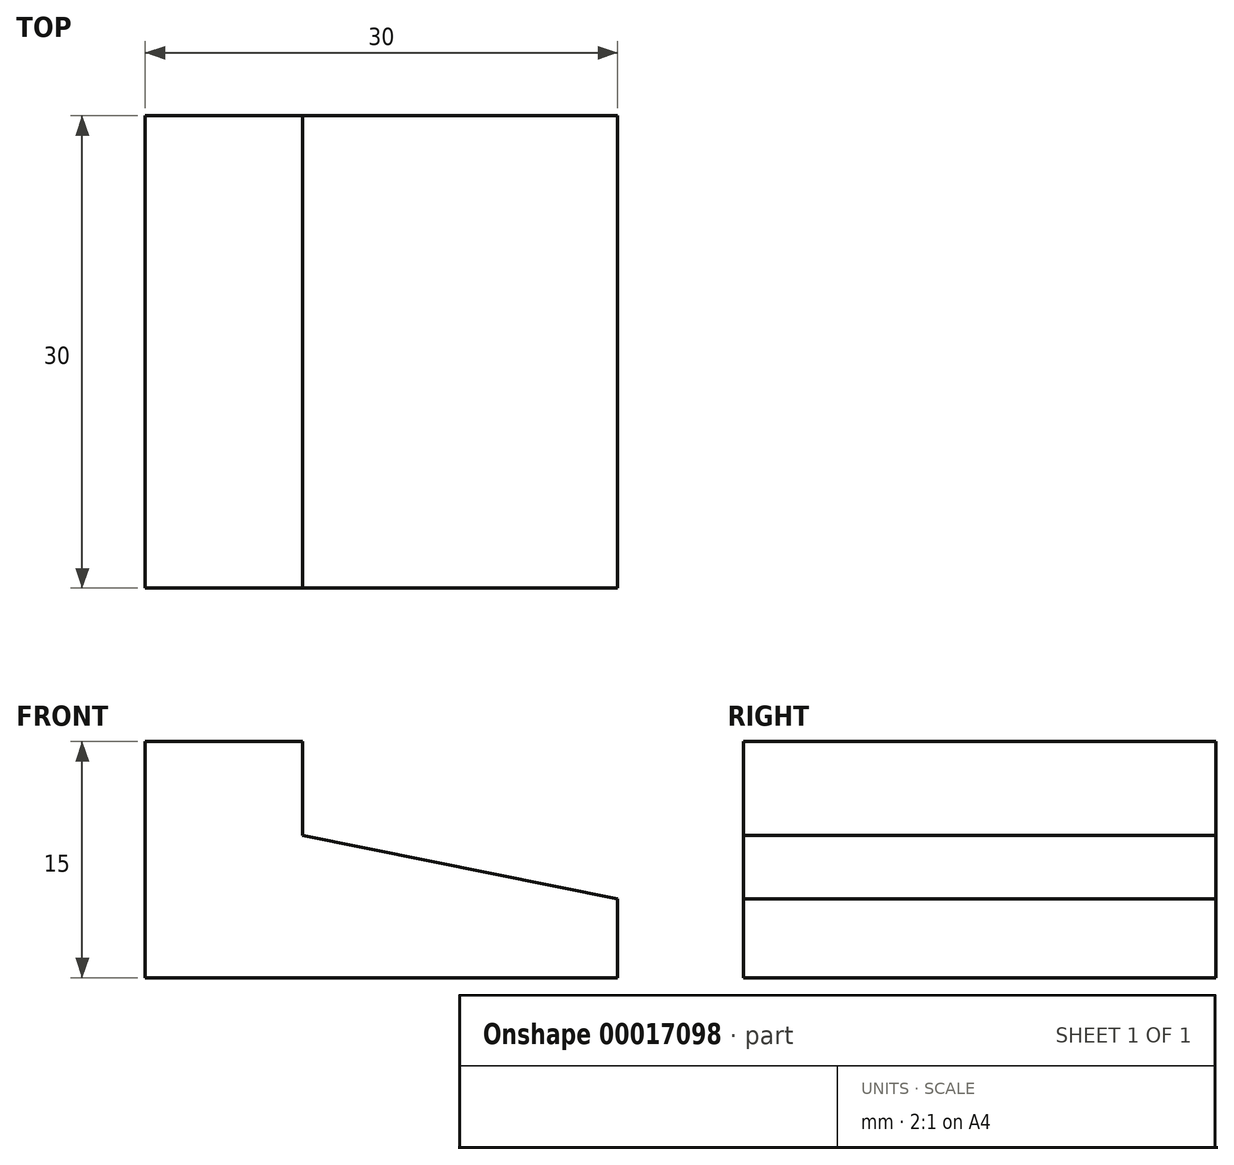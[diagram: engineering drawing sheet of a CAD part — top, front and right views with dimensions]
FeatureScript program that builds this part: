
annotation { "Feature Type Name" : "Feature", "Feature Type Description" : "" }
export const myFeature = defineFeature(function(context is Context, id is Id, definition is map)
    precondition{}
    {
        {
            var Q0;
            Q0=qCreatedBy(makeId("Front.planeOp"),FACE);
            var sketch = newSketch(context, id + "F0", { "sketchPlane" : qUnion([Q0])});
            skLineSegment(sketch, "E0", {"start": v(5.16, 8.93) * mm, "end": v(-4.84, 8.93) * mm});
            skLineSegment(sketch, "E1", {"start": v(-4.84, 8.93) * mm, "end": v(-4.84, -6.07) * mm});
            skLineSegment(sketch, "E2", {"start": v(-4.84, -6.07) * mm, "end": v(25.16, -6.07) * mm});
            skLineSegment(sketch, "E3", {"start": v(25.16, -1.07) * mm, "end": v(25.16, -6.07) * mm});
            skLineSegment(sketch, "E4", {"start": v(5.16, 8.93) * mm, "end": v(5.16, 2.99) * mm});
            skLineSegment(sketch, "E5", {"start": v(5.16, 2.99) * mm, "end": v(25.16, -1.07) * mm});
            skSolve(sketch);
        }
        {
            var Q0;
            Q0=makeQuery(id+"F0.imprint","IMPRINT",FACE,{"disambiguationData":[TD([[makeQuery(id+"F0.imprint","IMPRINT",EDGE,{"derivedFrom":sQuery(id+"F0.wireOp",EDGE,"E0")}),1.0]])]});
            extrude(context, id + "F1", {"entities" : qUnion([Q0]), "depth" : 30 * mm});
        }
    });
